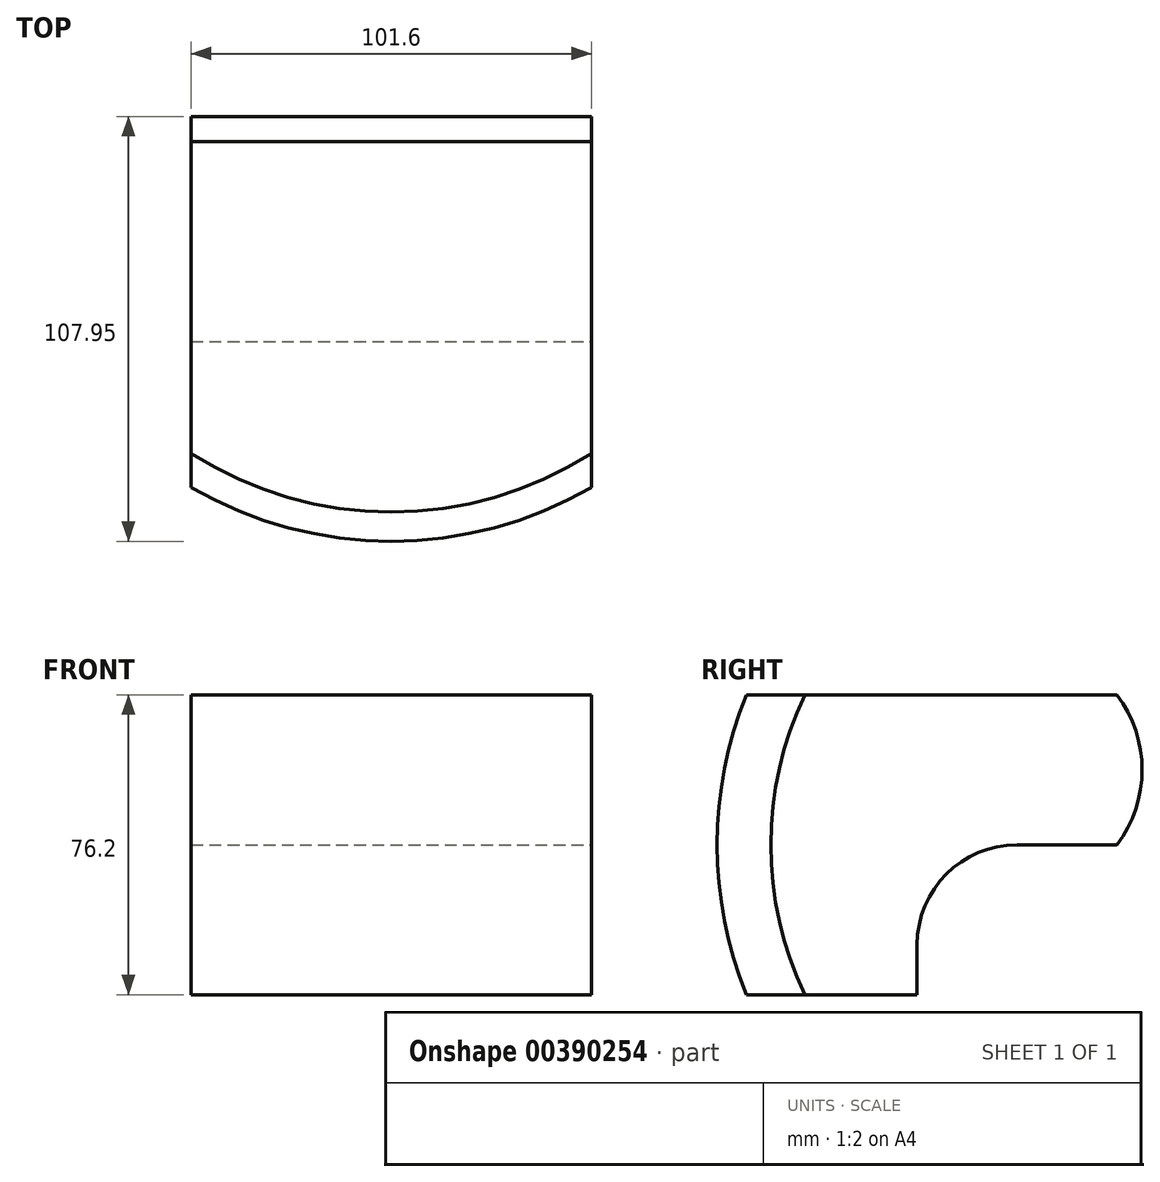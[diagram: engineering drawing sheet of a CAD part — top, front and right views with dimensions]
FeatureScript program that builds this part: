
annotation { "Feature Type Name" : "Feature", "Feature Type Description" : "" }
export const myFeature = defineFeature(function(context is Context, id is Id, definition is map)
    precondition{}
    {
        {
            var Q0;
            Q0=qCreatedBy(makeId("Top.planeOp"),FACE);
            var sketch = newSketch(context, id + "F0", { "sketchPlane" : qUnion([Q0])});
            skLineSegment(sketch, "E0.bottom", {"start": v(50.8, -50.8) * mm, "end": v(-50.8, -50.8) * mm});
            skLineSegment(sketch, "E0.top", {"start": v(50.8, 50.8) * mm, "end": v(-50.8, 50.8) * mm});
            skLineSegment(sketch, "E0.left", {"start": v(50.8, -50.8) * mm, "end": v(50.8, 50.8) * mm});
            skLineSegment(sketch, "E0.right", {"start": v(-50.8, -50.8) * mm, "end": v(-50.8, 50.8) * mm});
            skPoint(sketch, "E0.middle", {"position": v(0, 0) * mm});
            skSolve(sketch);
        }
        {
            var Q0;
            Q0 = qSketchRegion(id + "F0", true);
            extrude(context, id + "F1", {"entities" : qUnion([Q0]), "endBound" : BoundingType.SYMMETRIC, "depth" : 76.2 * mm});
        }
        {
            var Q0;
            Q0=makeQuery(id+"F1.opExtrude","SWEPT_FACE",FACE,{"disambiguationData":[OSD([sQuery(id+"F0.wireOp",EDGE,"E0.top")])]});
            var sketch = newSketch(context, id + "F2", { "sketchPlane" : qUnion([Q0])});
            skLineSegment(sketch, "E1", {"start": v(0, 38.1) * mm, "end": v(0, -38.1) * mm, "construction": true});
            skSolve(sketch);
        }
        {
            var Q0;
            Q0=qCreatedBy(makeId("Right.planeOp"),FACE);
            var sketch = newSketch(context, id + "F3", { "sketchPlane" : qUnion([Q0])});
            skPoint(sketch, "E2.endSnap0", {"position": v(0, -38.1) * mm});
            skLineSegment(sketch, "E3", {"start": v(0, -38.1) * mm, "end": v(0, -25.4) * mm});
            skLineSegment(sketch, "E4", {"start": v(50.8, 0) * mm, "end": v(25.4, 0) * mm});
            skArc(sketch, "E5", {"start": v(25.4, 0) * mm, "mid": v(7.44, -7.44) * mm, "end": v(0, -25.4) * mm});
            skArc(sketch, "E6", {"start": v(-43.39, 38.1) * mm, "mid": v(-50.8, 0) * mm, "end": v(-43.39, -38.1) * mm});
            skLineSegment(sketch, "E7", {"start": v(-43.39, 38.1) * mm, "end": v(-68.79, 38.1) * mm});
            skLineSegment(sketch, "E8", {"start": v(-43.39, -38.1) * mm, "end": v(-68.79, -38.1) * mm});
            skLineSegment(sketch, "E9", {"start": v(0, -38.1) * mm, "end": v(50.8, -38.1) * mm});
            skLineSegment(sketch, "E10", {"start": v(50.8, -38.1) * mm, "end": v(50.8, 0) * mm});
            skLineSegment(sketch, "E11", {"start": v(-68.79, 38.1) * mm, "end": v(-68.79, -38.1) * mm});
            skArc(sketch, "E12", {"start": v(50.8, 0) * mm, "mid": v(57.15, 19.05) * mm, "end": v(50.8, 38.1) * mm});
            skLineSegment(sketch, "E13", {"start": v(50.8, 38.1) * mm, "end": v(50.8, 0) * mm});
            skSolve(sketch);
        }
        {
            var Q0;
            {var subQ5=sQuery(id+"F3.wireOp",EDGE,"E3");Q0=makeQuery(id+"F3.imprint","IMPRINT",FACE,{"disambiguationData":[TD([[makeQuery(id+"F3.imprint","IMPRINT",EDGE,{"derivedFrom":subQ5}),-1.0]])]});}
            extrude(context, id + "F4", {"entities" : qUnion([Q0]), "operationType" : NewBodyOperationType.REMOVE, "endBound" : BoundingType.SYMMETRIC, "oppositeDirection" : true, "depth" : 101.6 * mm});
        }
        {
            var Q0;
            Q0=makeQuery(id+"F3.imprint","IMPRINT",FACE,{"disambiguationData":[TD([[makeQuery(id+"F3.imprint","IMPRINT",EDGE,{"derivedFrom":sQuery(id+"F3.wireOp",EDGE,"E6")}),-1.0]])]});
            var Q1;
            Q1=sQuery(id+"F2.wireOp",EDGE,"E1");
            revolve(context, id + "F5", {"operationType" : NewBodyOperationType.REMOVE, "entities" : qUnion([Q0]), "axis" : qUnion([Q1]), "revolveType" : RevolveType.SYMMETRIC, "angle" : 70 * degree});
        }
        {
            var Q0;
            Q0=makeQuery(id+"F3.imprint","IMPRINT",FACE,{"disambiguationData":[TD([[makeQuery(id+"F3.imprint","IMPRINT",EDGE,{"derivedFrom":sQuery(id+"F3.wireOp",EDGE,"E12")}),1.0]])]});
            extrude(context, id + "F6", {"entities" : qUnion([Q0]), "operationType" : NewBodyOperationType.ADD, "endBound" : BoundingType.SYMMETRIC, "depth" : 101.6 * mm});
        }
    });
